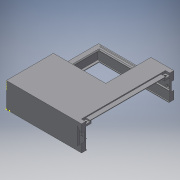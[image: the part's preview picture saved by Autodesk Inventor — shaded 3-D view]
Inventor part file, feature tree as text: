
AUTODESK INVENTOR PART (.ipt)
format: ipt  version: 2016 SP2 (Build 200236200, 236)  size: 865,280 bytes
history: native  units: mm
features: sketch x29, other x5, thread x2, revolve x2
ambient origin geometry x8: Origin, YZ Plane, XZ Plane, XY Plane, X Axis, Y Axis, Z Axis, Center Point
bodies: Volumenkörper2 (feature_tree), Volumenkörper3 (feature_tree), Volumenkörper1 (feature_tree)
feature tree (38):
  other  "Bauteil1.ipt"
  thread  "Gewinde1"  [1 undecoded]
  thread  "Gewinde2"  [1 undecoded]
  revolve  "Umdrehung1"
  other  "Spirale1"
  revolve  "Umdrehung2"
  other  "Spirale2"
  other  "Volumenkörper1::Bauteil1.ipt"
  other  "Bezeichnung1"
  sketch  "Skizze1"  dims[d3=10.0mm d4=0.0mm]
  sketch  "Skizze2"  dims[d5=60.0deg d6=0.240125mm d7=0.240125mm]
  sketch  "Skizze3"  dims[d10=1.5mm]
  sketch  "Skizze4"  dims[d12=60.0deg]
  sketch  "Skizze5"  dims[d14=0.0mm]
  sketch  "Skizze6"  dims[d15=1.5015mm d16=8.0mm d17=10.0mm d18=0.0mm d19=0.0mm d20=0.0mm d21=0.0mm d22=0.0mm]
  sketch  "Skizze7"  dims[d23=60.0deg d24=0.240125mm d25=0.240125mm]
  sketch  "Skizze8"  dims[d28=1.5mm]
  sketch  "Skizze9"  dims[d30=60.0deg]
  sketch  "Skizze10"  dims[d32=0.0mm]
  sketch  "Skizze11"  dims[d33=1.5015mm d34=8.0mm d35=10.0mm d36=0.0mm d37=0.0mm d38=0.0mm d39=0.0mm d40=0.0mm]
  sketch  "Skizze13"
  sketch  "Skizze14"
  sketch  "Skizze15"
  sketch  "Skizze16"
  sketch  "Skizze17"
  sketch  "Skizze19"
  sketch  "Skizze21"
  sketch  "Skizze22"
  sketch  "Skizze23"
  sketch  "Skizze24"
  sketch  "Skizze25"
  sketch  "Skizze26"
  sketch  "Skizze27"
  sketch  "Skizze28"
  sketch  "Skizze29"
  sketch  "Skizze30"
  sketch  "Skizze31"
  sketch  "Skizze32"
note: 2 required parameter values undecoded (feature->parameter linkage not recoverable at this tier; creation-order binding heuristic only, values carry confidence <= 0.55)
